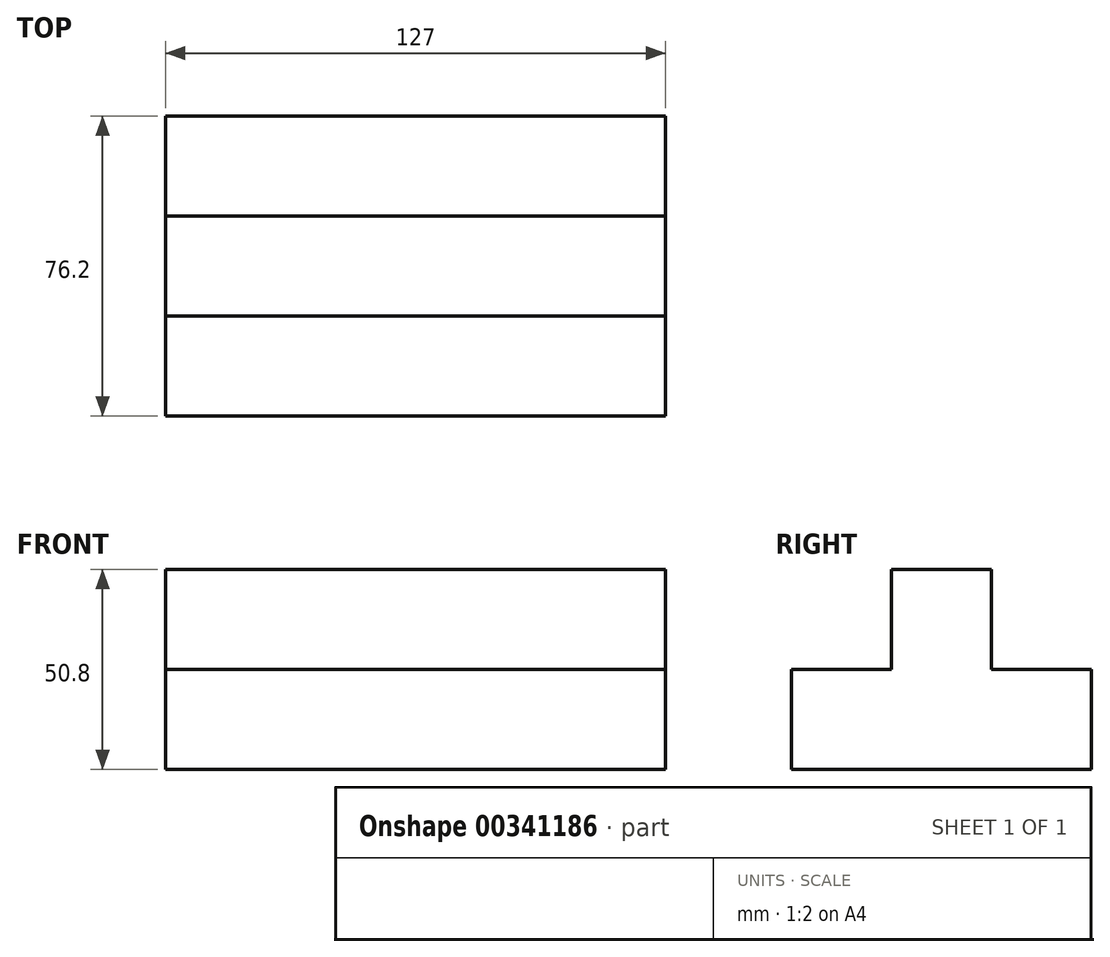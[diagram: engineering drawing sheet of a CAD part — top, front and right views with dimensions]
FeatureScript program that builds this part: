
annotation { "Feature Type Name" : "Feature", "Feature Type Description" : "" }
export const myFeature = defineFeature(function(context is Context, id is Id, definition is map)
    precondition{}
    {
        {
            var Q0;
            Q0=qCreatedBy(makeId("Right.planeOp"),FACE);
            var sketch = newSketch(context, id + "F0", { "sketchPlane" : qUnion([Q0])});
            skLineSegment(sketch, "E0", {"start": v(0, 0) * mm, "end": v(0, 25.4) * mm});
            skLineSegment(sketch, "E1", {"start": v(0, 25.4) * mm, "end": v(25.4, 25.4) * mm});
            skLineSegment(sketch, "E2", {"start": v(25.4, 25.4) * mm, "end": v(25.4, 50.8) * mm});
            skLineSegment(sketch, "E3", {"start": v(25.4, 50.8) * mm, "end": v(50.8, 50.8) * mm});
            skLineSegment(sketch, "E4", {"start": v(50.8, 50.8) * mm, "end": v(50.8, 25.4) * mm});
            skLineSegment(sketch, "E5", {"start": v(50.8, 25.4) * mm, "end": v(76.2, 25.4) * mm});
            skLineSegment(sketch, "E6", {"start": v(76.2, 25.4) * mm, "end": v(76.2, 0) * mm});
            skLineSegment(sketch, "E7", {"start": v(76.2, 0) * mm, "end": v(0, 0) * mm});
            skSolve(sketch);
        }
        {
            var Q0;
            Q0 = qSketchRegion(id + "F0", true);
            extrude(context, id + "F1", {"entities" : qUnion([Q0]), "depth" : 127 * mm});
        }
    });
